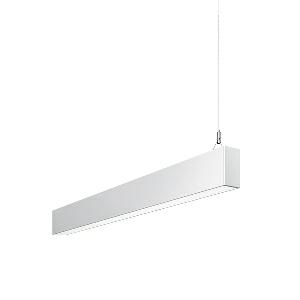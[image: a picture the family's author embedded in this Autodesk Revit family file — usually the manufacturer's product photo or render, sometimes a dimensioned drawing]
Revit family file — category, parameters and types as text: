
# Revit family: idoo_line_-_ilp_4000_840_d_end_00805698_3dd4
name_source: partatom
category: Lighting Fixtures
units: mm (PartAtom-declared; Revit-internal decimal feet)

## family parameters
Cut with Voids When Loaded = No
Host = Face
Light Source = No
Part Type = Normal
Room Calculation Point = No
Round Connector Dimension = Use Diameter
Shared = No

## types (1)
- IDOO.line - ILP 4000/840/D END (1 x LED, 3950 lm, 4000K)
    Apparent Load = 29 VA
    Approval mark = CE
    CIE Flux Codes = 66 91 98 40 100
    Color Rendering = 80-89
    Color Temperature = 4000K
    Control Gear = Electronic ballast
    Default Elevation = 1800 mm
    Description = ILP 4000/840/D|Suspended luminaire|light source: LED|connected load: 220-240 V, 50/60 Hz|Power consumption: approx. 29 W|standby: approx. 0,15|luminous flux: 3950 lm|luminous efficacy: 136 lm/W|light distribution: Direct/indirect|direct ratio: approx. 40 %|colour temperature: Cold white, ca. 4000 K|color rendering index (CRI): >= 80|chromaticity tolerance:  3 SDCM|System of protection: IP 40|technology: Continuously dimmable|luminaire body|material: Sectional aluminium|colour: White|lamp cover: Acrylic (PMMA), Clear|mains lead: 1,0 m With free stranded wires|Fastening: Steel cable 0.3 - 0.7 m|glare control: Prism aperture|luminance(L65): <= 2700 cd/m|unified glare rating(4H 8H): <=  16|special features: DALI Load 1x, TouchDIM - dimming via standard switch, Through-wired, up to 18 m on one mains connection, Flicker-free, Suitable as emergency lighting, Mechanical and electrical connection of the individual modules without tools|
    Frequency = 50 Hz
    Height = 110 mm
    Lamp = 1 x LED
    Lamp Light Flux = 3950 lm
    Lamp count = 1
    Length = 1408 mm
    Luminous efficacy = 136 lm/W
    Manufacturer = Waldmann
    ModVariant = No
    Model = 00805698
    Mounting Place = Ceiling
    Mounting Type = Pendant
    Number of Poles = 1
    OnlyDefault = Yes
    Power Factor = 1
    Product Name = IDOO.line - ILP 4000/840/D END
    Product group = Suspended luminaire
    ProductGroupID = 9
    Protection Class = Protection class I
    Protection Degree = IP 40
    RLX_Detail_Level = 1
    RLX_Emergency_Light_Flux = 0 lm
    RLX_Emergency_Type = 0
    RLX_Emergency_Type_DB = No
    RlxData = <blob elided: 18649 chars, md5=15ca9f51>
    Socket = socket
    Standby Power = 0 W
    System Light Flux = 3950 lm
    System Power = 29 W
    Type Comments = Product without accessories
    Type Image = 113309000-00692591.jpg
    URL = http://relux.com
    VarID = ---
    Voltage = 230 V
    Voltage Range = 220-240 V
    Weight = 0.00 kg
    Width = 60 mm  [stored 0.19685 ft]

note: [stored X ft] marks values corroborated as IEEE doubles in the binary element streams (Revit-internal decimal feet)

## geometry (parser evidence)
native form markers: Blend x4, Sweep x12
no freeform markers — native parametric forms only
